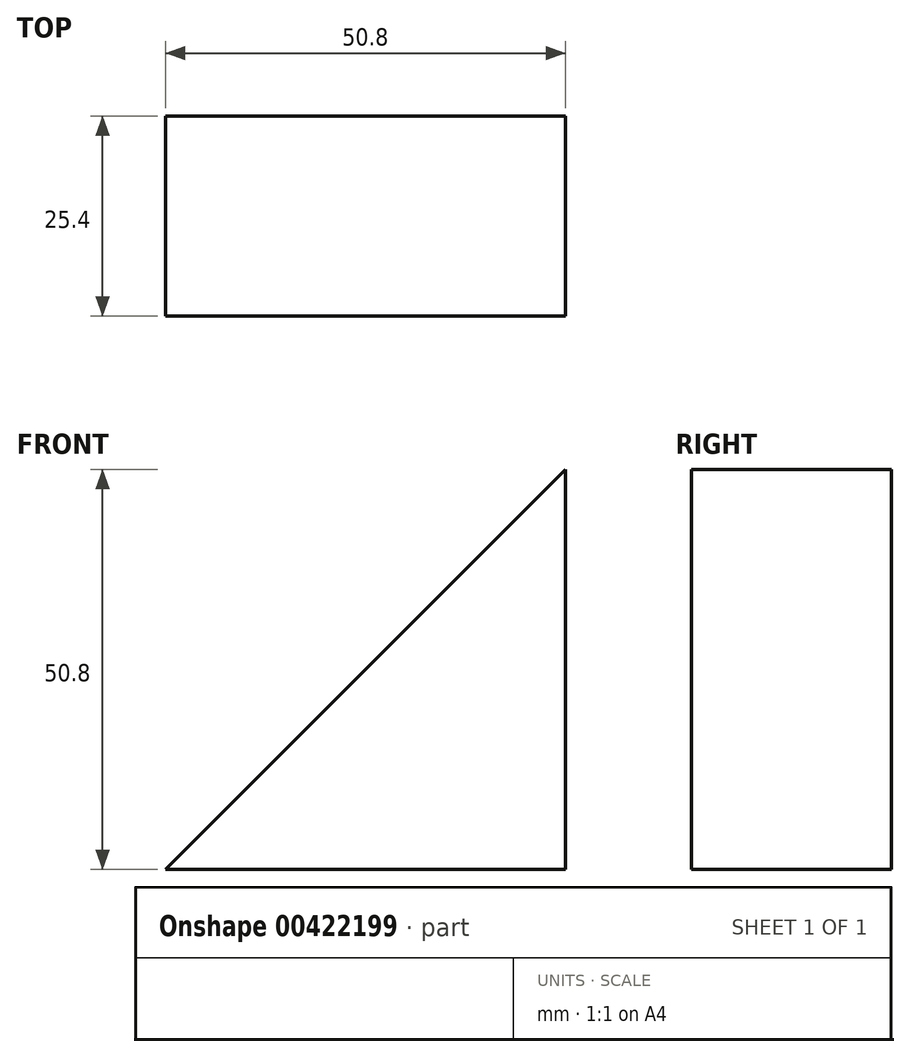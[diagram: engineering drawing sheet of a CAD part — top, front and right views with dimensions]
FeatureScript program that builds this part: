
annotation { "Feature Type Name" : "Feature", "Feature Type Description" : "" }
export const myFeature = defineFeature(function(context is Context, id is Id, definition is map)
    precondition{}
    {
        {
            var Q0;
            Q0=qCreatedBy(makeId("Front.planeOp"),FACE);
            var sketch = newSketch(context, id + "F0", { "sketchPlane" : qUnion([Q0])});
            skLineSegment(sketch, "E0", {"start": v(0, 0) * mm, "end": v(-50.8, 0) * mm});
            skLineSegment(sketch, "E1", {"start": v(0, 0) * mm, "end": v(0, 50.8) * mm});
            skLineSegment(sketch, "E2", {"start": v(0, 50.8) * mm, "end": v(-50.8, 0) * mm});
            skSolve(sketch);
        }
        {
            var Q0;
            Q0=makeQuery(id+"F0.imprint","IMPRINT",FACE,{"disambiguationData":[TD([[makeQuery(id+"F0.imprint","IMPRINT",EDGE,{"derivedFrom":sQuery(id+"F0.wireOp",EDGE,"E0")}),-1.0]])]});
            extrude(context, id + "F1", {"entities" : qUnion([Q0]), "depth" : 25.4 * mm});
        }
    });
